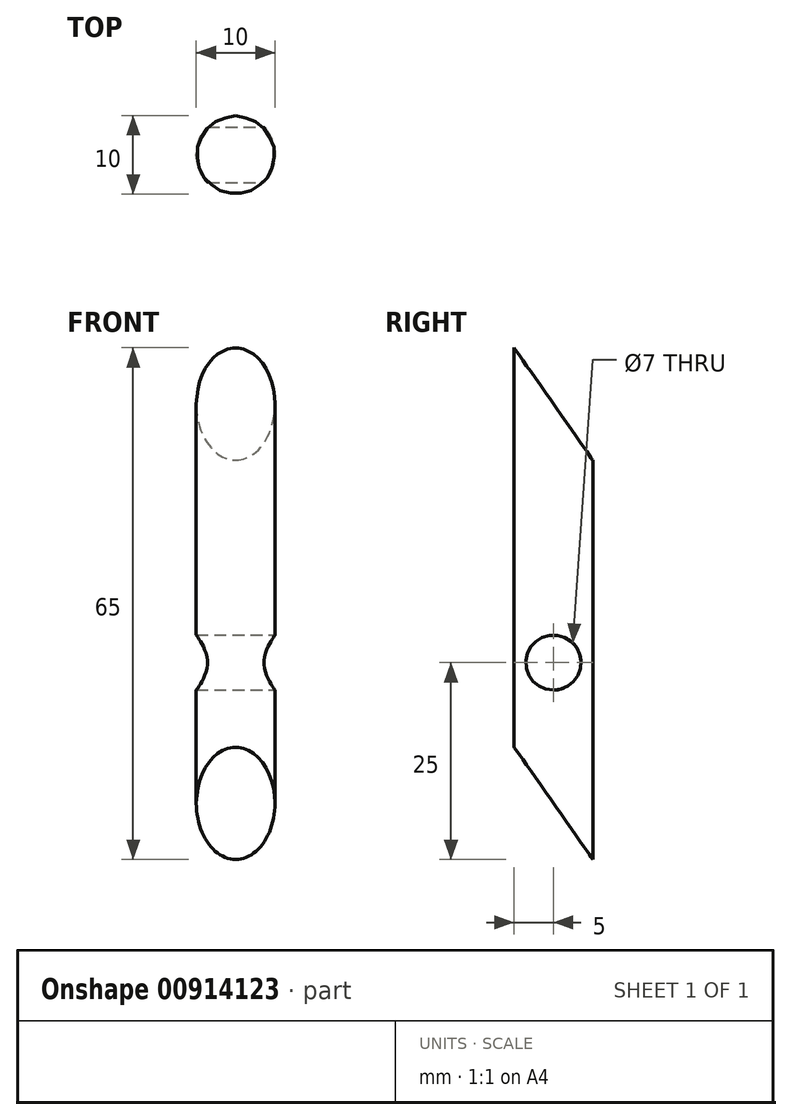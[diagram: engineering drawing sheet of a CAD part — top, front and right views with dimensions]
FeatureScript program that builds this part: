
annotation { "Feature Type Name" : "Feature", "Feature Type Description" : "" }
export const myFeature = defineFeature(function(context is Context, id is Id, definition is map)
    precondition{}
    {
        {
            var Q0;
            Q0=qCreatedBy(makeId("Top.planeOp"),FACE);
            var sketch = newSketch(context, id + "F0", { "sketchPlane" : qUnion([Q0])});
            skCircle(sketch, "E0", {"center": v(0, 0) * mm, "radius": 5 * mm});
            skSolve(sketch);
        }
        {
            var Q0;
            Q0 = qSketchRegion(id + "F0", true);
            extrude(context, id + "F1", {"entities" : qUnion([Q0]), "depth" : 65 * mm, "offsetDistance" : 25 * mm});
        }
        {
            var Q0;
            Q0=qCreatedBy(makeId("Right.planeOp"),FACE);
            var sketch = newSketch(context, id + "F2", { "sketchPlane" : qUnion([Q0])});
            skLineSegment(sketch, "E1", {"start": v(-5, 0) * mm, "end": v(-5, 14.28) * mm});
            skLineSegment(sketch, "E2", {"start": v(5, 65) * mm, "end": v(5, 50.72) * mm});
            skLineSegment(sketch, "E3.0", {"start": v(-5, 0) * mm, "end": v(5, 0) * mm});
            skLineSegment(sketch, "E4.0", {"start": v(-5, 65) * mm, "end": v(5, 65) * mm});
            skLineSegment(sketch, "E5", {"start": v(5, 0) * mm, "end": v(-5, 14.28) * mm});
            skLineSegment(sketch, "E6", {"start": v(-5, 65) * mm, "end": v(5, 50.72) * mm});
            skCircle(sketch, "E7", {"center": v(0, 25) * mm, "radius": 3.5 * mm});
            skSolve(sketch);
        }
        {
            var Q0;
            Q0 = qSketchRegion(id + "F2", true);
            extrude(context, id + "F3", {"entities" : qUnion([Q0]), "operationType" : NewBodyOperationType.REMOVE, "endBound" : BoundingType.UP_TO_NEXT, "oppositeDirection" : true, "depth" : 25 * mm, "offsetDistance" : 25 * mm, "hasSecondDirection" : true, "secondDirectionBound" : BoundingType.UP_TO_NEXT, "secondDirectionOppositeDirection" : false, "secondDirectionDepth" : 25 * mm});
        }
    });
